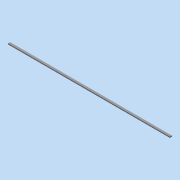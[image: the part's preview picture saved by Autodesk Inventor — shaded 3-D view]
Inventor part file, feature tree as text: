
AUTODESK INVENTOR PART (.ipt)
format: ipt  version: 2015 (Build 190159000, 159)  size: 66,048 bytes
history: native  units: in
note: dims shown in document units (in); Inventor stores cm internally (conversion verified against a paired STEP export)
features: extrude x1, sketch x1
ambient origin geometry x8: Origin, YZ Plane, XZ Plane, XY Plane, X Axis, Y Axis, Z Axis, Center Point
bodies: Solid1 (feature_tree)
feature tree (2):
  extrude  "Extrusion1"  Depth=0.05in
  sketch  "Sketch1"  dims[d0=4.0in d1=0.05in d2=0.025in d3=0.0in]
